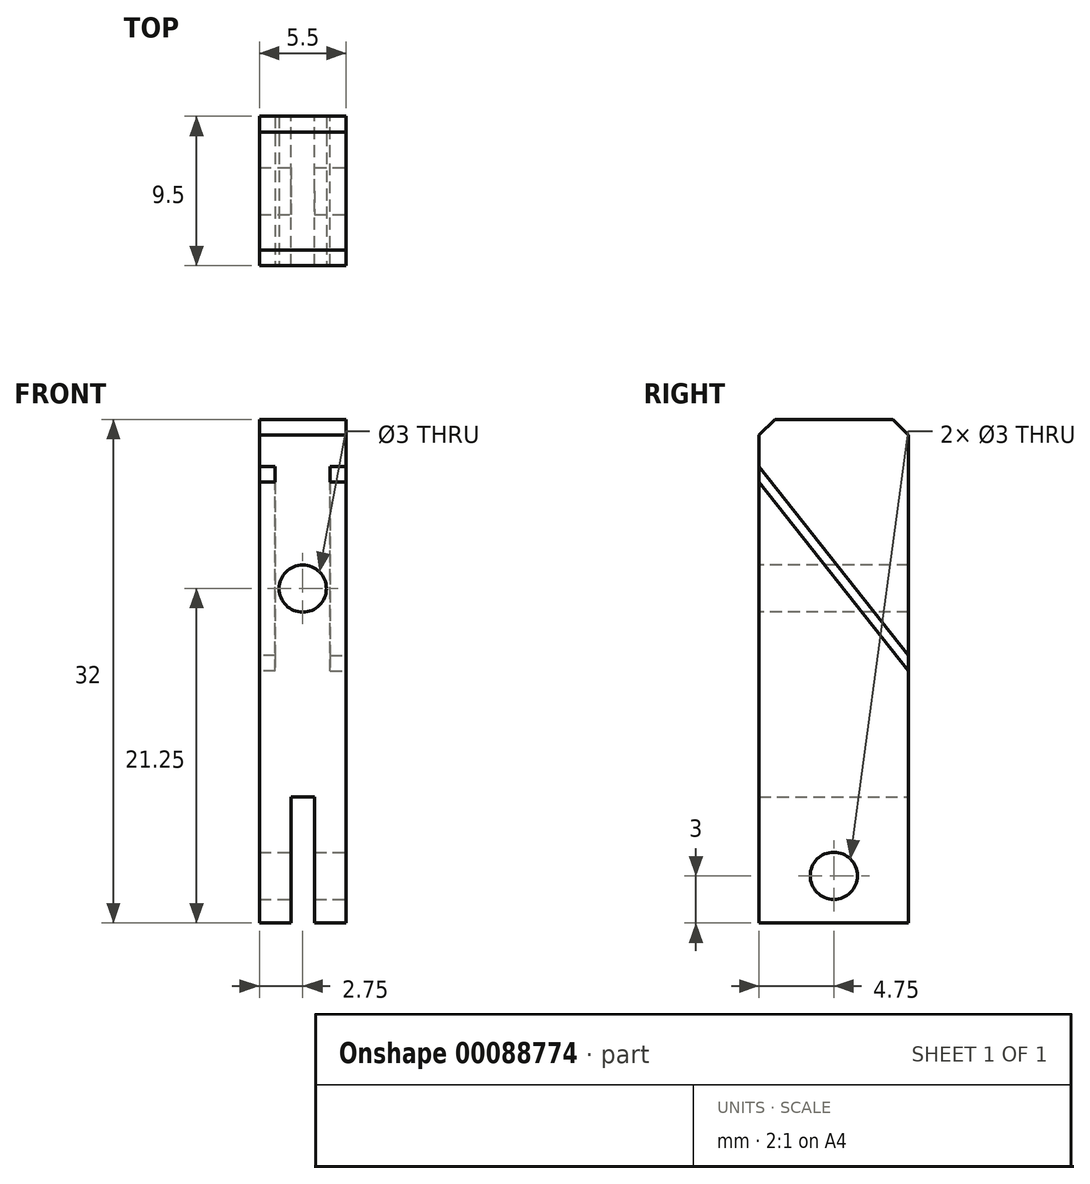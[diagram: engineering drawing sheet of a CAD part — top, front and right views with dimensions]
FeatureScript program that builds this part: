
annotation { "Feature Type Name" : "Feature", "Feature Type Description" : "" }
export const myFeature = defineFeature(function(context is Context, id is Id, definition is map)
    precondition{}
    {
        {
            var Q0;
            Q0=qCreatedBy(makeId("Top.planeOp"),FACE);
            var sketch = newSketch(context, id + "F0", { "sketchPlane" : qUnion([Q0])});
            skLineSegment(sketch, "E0.bottom", {"start": v(0, 0) * mm, "end": v(5.5, 0) * mm});
            skLineSegment(sketch, "E0.top", {"start": v(0, 9.5) * mm, "end": v(5.5, 9.5) * mm});
            skLineSegment(sketch, "E0.left", {"start": v(0, 0) * mm, "end": v(0, 9.5) * mm});
            skLineSegment(sketch, "E0.right", {"start": v(5.5, 0) * mm, "end": v(5.5, 9.5) * mm});
            skSolve(sketch);
        }
        {
            var Q0;
            Q0 = qSketchRegion(id + "F0", true);
            extrude(context, id + "F1", {"entities" : qUnion([Q0]), "depth" : 32 * mm});
        }
        {
            var Q0;
            Q0=makeQuery(id+"F1.opExtrude","CAP_EDGE",EDGE,{"disambiguationData":[OSD([sQuery(id+"F0.wireOp",EDGE,"E0.bottom")])],"isStart":false});
            var Q1;
            Q1=makeQuery(id+"F1.opExtrude","CAP_EDGE",EDGE,{"disambiguationData":[OSD([sQuery(id+"F0.wireOp",EDGE,"E0.top")])],"isStart":false});
            chamfer(context, id + "F2", {"entities" : qUnion([Q0, Q1]), "width" : 1 * mm, "tangentPropagation" : true});
        }
        {
            var Q0;
            Q0=makeQuery(id+"F1.opExtrude","SWEPT_FACE",FACE,{"disambiguationData":[OSD([sQuery(id+"F0.wireOp",EDGE,"E0.right")])]});
            var sketch = newSketch(context, id + "F3", { "sketchPlane" : qUnion([Q0])});
            skLineSegment(sketch, "E1", {"start": v(4.75, 0) * mm, "end": v(4.75, 3) * mm, "construction": true});
            skCircle(sketch, "E2", {"center": v(4.75, 3) * mm, "radius": 1.5 * mm});
            skSolve(sketch);
        }
        {
            var Q0;
            Q0 = qSketchRegion(id + "F3", true);
            var Q1;
            Q1=makeQuery(id+"F1.opExtrude","SWEPT_FACE",FACE,{"disambiguationData":[OSD([sQuery(id+"F0.wireOp",EDGE,"E0.left")])]});
            extrude(context, id + "F4", {"entities" : qUnion([Q0]), "operationType" : NewBodyOperationType.REMOVE, "endBound" : BoundingType.UP_TO_SURFACE, "oppositeDirection" : true, "endBoundEntityFace" : qUnion([Q1]), "depth" : 25 * mm});
        }
        {
            var Q0;
            Q0=makeQuery(id+"F1.opExtrude","SWEPT_FACE",FACE,{"disambiguationData":[OSD([sQuery(id+"F0.wireOp",EDGE,"E0.top")])]});
            var sketch = newSketch(context, id + "F5", { "sketchPlane" : qUnion([Q0])});
            skLineSegment(sketch, "E3", {"start": v(-2.75, 0) * mm, "end": v(-2.75, 4) * mm, "construction": true});
            skLineSegment(sketch, "E4.bottom", {"start": v(-3.5, 0) * mm, "end": v(-2, 0) * mm});
            skLineSegment(sketch, "E4.top", {"start": v(-3.5, 8) * mm, "end": v(-2, 8) * mm});
            skLineSegment(sketch, "E4.left", {"start": v(-3.5, 0) * mm, "end": v(-3.5, 8) * mm});
            skLineSegment(sketch, "E4.right", {"start": v(-2, 0) * mm, "end": v(-2, 8) * mm});
            skPoint(sketch, "E4.middle", {"position": v(-2.75, 4) * mm});
            skSolve(sketch);
        }
        {
            var Q0;
            Q0 = qSketchRegion(id + "F5", true);
            var Q1;
            Q1=makeQuery(id+"F1.opExtrude","SWEPT_FACE",FACE,{"disambiguationData":[OSD([sQuery(id+"F0.wireOp",EDGE,"E0.bottom")])]});
            extrude(context, id + "F6", {"entities" : qUnion([Q0]), "operationType" : NewBodyOperationType.REMOVE, "endBound" : BoundingType.UP_TO_SURFACE, "oppositeDirection" : true, "endBoundEntityFace" : qUnion([Q1]), "depth" : 25 * mm});
        }
        {
            var Q0;
            Q0=makeQuery(id+"F1.opExtrude","SWEPT_FACE",FACE,{"disambiguationData":[OSD([sQuery(id+"F0.wireOp",EDGE,"E0.right")])]});
            var sketch = newSketch(context, id + "F7", { "sketchPlane" : qUnion([Q0])});
            skLineSegment(sketch, "E5", {"start": v(0, 29) * mm, "end": v(9.5, 17) * mm});
            skLineSegment(sketch, "E6", {"start": v(9.5, 17) * mm, "end": v(9.5, 16) * mm});
            skLineSegment(sketch, "E7", {"start": v(9.5, 16) * mm, "end": v(0, 28) * mm});
            skLineSegment(sketch, "E8", {"start": v(0, 28) * mm, "end": v(0, 29) * mm});
            skSolve(sketch);
        }
        {
            var Q0;
            Q0 = qSketchRegion(id + "F7", true);
            extrude(context, id + "F8", {"entities" : qUnion([Q0]), "operationType" : NewBodyOperationType.REMOVE, "oppositeDirection" : true, "depth" : 1 * mm});
        }
        {
            var Q0;
            Q0=makeQuery(id+"F1.opExtrude","SWEPT_FACE",FACE,{"disambiguationData":[OSD([sQuery(id+"F0.wireOp",EDGE,"E0.left")])]});
            var sketch = newSketch(context, id + "F9", { "sketchPlane" : qUnion([Q0])});
            skLineSegment(sketch, "E9.0", {"start": v(0, 29) * mm, "end": v(0, 28) * mm});
            skLineSegment(sketch, "E9.1", {"start": v(-9.5, 16) * mm, "end": v(0, 28) * mm});
            skLineSegment(sketch, "E9.2", {"start": v(0, 29) * mm, "end": v(-9.5, 17) * mm});
            skLineSegment(sketch, "E9.3", {"start": v(-9.5, 17) * mm, "end": v(-9.5, 16) * mm});
            skSolve(sketch);
        }
        {
            var Q0;
            Q0 = qSketchRegion(id + "F9", true);
            extrude(context, id + "F10", {"entities" : qUnion([Q0]), "operationType" : NewBodyOperationType.REMOVE, "oppositeDirection" : true, "depth" : 1 * mm});
        }
        {
            var Q0;
            Q0=makeQuery(id+"F1.opExtrude","SWEPT_FACE",FACE,{"disambiguationData":[OSD([sQuery(id+"F0.wireOp",EDGE,"E0.bottom")])]});
            var sketch = newSketch(context, id + "F11", { "sketchPlane" : qUnion([Q0])});
            skLineSegment(sketch, "E10", {"start": v(2.75, 31) * mm, "end": v(2.75, 21.25) * mm, "construction": true});
            skLineSegment(sketch, "E11.0", {"start": v(0, 32) * mm, "end": v(5.5, 32) * mm, "construction": true});
            skCircle(sketch, "E12", {"center": v(2.75, 21.25) * mm, "radius": 1.5 * mm});
            skSolve(sketch);
        }
        {
            var Q0;
            Q0 = qSketchRegion(id + "F11", true);
            var Q1;
            Q1=makeQuery(id+"F1.opExtrude","SWEPT_FACE",FACE,{"disambiguationData":[OSD([sQuery(id+"F0.wireOp",EDGE,"E0.top")])]});
            extrude(context, id + "F12", {"entities" : qUnion([Q0]), "operationType" : NewBodyOperationType.REMOVE, "endBound" : BoundingType.UP_TO_SURFACE, "oppositeDirection" : true, "endBoundEntityFace" : qUnion([Q1]), "depth" : 25 * mm});
        }
    });
